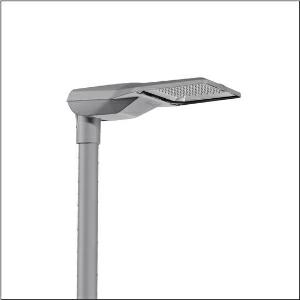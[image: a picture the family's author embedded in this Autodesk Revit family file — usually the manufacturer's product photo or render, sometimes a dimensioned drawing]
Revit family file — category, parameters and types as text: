
# Revit family: streetlight_sl_21_iq_midi___st0_5a_5xe3b31d08mb_db69
name_source: partatom
category: Lighting Fixtures
units: mm (PartAtom-declared; Revit-internal decimal feet)

## family parameters
Cut with Voids When Loaded = No
Host = Face
Light Source = No
Part Type = Normal
Room Calculation Point = No
Round Connector Dimension = Use Diameter
Shared = No

## types (1)
- --- (1 x LED, 19500 lm, 146.7 W, 3000K)
    Apparent Load = 147 VA
    CIE Flux Codes = 41 75 97 100 100
    Color Rendering = 70
    Color Temperature = 3000K
    Default Elevation = 1800 mm
    Description = Streetlight SL 21 iQ midi, mast luminaire, primary light control with lens, of PMMA, primary optical cover: cover, of toughened safety glass, transparent, light distribution: ST0.5a, light emission: direct distribution, primary light characteristic: asymmetric, installation type: post-top, side-entry, LED, High Power LED, rated luminous flux: 19.500lm, luminous efficacy: 133lm/W, light colour: 730, colour temperature: 3000K, control: Auto-Match, Temp-Guard, Lumen-Switch, Night-Set, Smart-Wire, Light-Fading, Desk-Remote (wireless, voltage-free reading and setting of iQ features in the workshop via application-optimized NFC function/RFID function), optimised constant luminous flux control (CLO 2.0), presetting dimming linear, mains connection: 230..240V, AC, 50/60Hz, start of lifetime: 147W, end of service life: 161W, reduction: 62W, luminaire housing, of diecast aluminium, powder-coated, Siteco® metallic grey (DB 702S), corrosivity category C5 mid according to DIN EN ISO 12944, please order mast flange separately, inclination adjustable: 0°, 5°, 10°, 15°, sealing non-destructively replaceable, multi-level sealing system, length: 644mm, width: 335mm, height: 110mm, mast flange for spigot size: 42mm (side-entry): 5XC10008XM4, 60/48mm (side-entry/post-top): 5XC10108XM2, 76/60mm (side-entry/post-top): 5XC10108XM1, protection rating (complete): IP66, insulation class (complete): insulation class II (safety insulation), certification: CE, ENEC, ENEC+, VDE, impact resistance: IK09, permissible operating ambient temperature for outdoor applications: -40..+50°C, standard-compliant lighting for roads and squares, packaging unit: 1 piece

Light Distribution: ST0.5a
    Height = 111 mm
    Lamp = 1 x LED
    Lamp Light Flux = 19500 lm
    Lamp Power = 146.7 W
    Lamp count = 1
    Length = 644 mm
    Luminous efficacy = 133 lm/W
    Manufacturer = Siteco
    ModVariant = No
    Model = 5XE3B31D08MB
    Number of Poles = 1
    OnlyDefault = Yes
    Power Factor = 1
    Product Name = Streetlight SL 21 iQ midi | ST0.5a
    Product group = mast luminaire | pylon top
    ProductGroupID = 6100
    Protection Class = Protection class II
    Protection Degree = IP 66
    RLX_Detail_Level = 1
    RLX_Emergency_Light_Flux = 0 lm
    RLX_Emergency_Type = 0
    RLX_Emergency_Type_DB = No
    RlxData = <blob elided: 102009 chars, md5=3e379326>
    Socket = socket
    Standby Power = 0 W
    System Light Flux = 19499 lm
    System Power = 147 W
    Type Comments = factory setting: luminous flux: 100 % | dim-lin: 254 | 753 mA
    Type Image = l_1004298.jpg
    URL = http://relux.com
    VarID = @adj_126169
    Voltage = 0 V
    Weight = 0.00 kg
    Width = 336 mm

## geometry (parser evidence)
native form markers: Blend x4, Sweep x11
no freeform markers — native parametric forms only
